# Revit family: 30391 Скамейка для запасных игроков на 5 посадочных мест с навесом «Брейк-5» Хоббика
name_source: partatom
category: Антураж
revit_build: Autodesk Revit 2018 (Build: 20180423_1000(x64)
units: mm (PartAtom-declared; Revit-internal decimal feet)

## family parameters
Всегда вертикально = Да
Источник визуального образа = Геометрия семейства
На основе рабочей плоскости = Нет
Общий = Нет
При загрузке вырезать с полостями = Нет
Точка расчета площади = Нет

## types (1)
- Скамейка для запасных игроков на 5 посадочных мест с навесом «Брейк-5»
    URL = https://hobbyka.ru
    Артикул товара = Арт. 30391
    Высота = 2150 мм
    Группа модели = Мобильные и стационарные трибуны
    Длина = 2840 мм
    Изготовитель = ООО «Хоббика»
    Изображение типоразмера = Скамейка для запасных игроков на 5 посадочных мест с навесом «Брейк-5» Арт 30391.jpg
    Материал изделия = Сталь, поликарбонат, пластик
    Описание = Скамейка для запасных игроков на 5 посадочных мест с навесом «Брейк-5»
    Цвет каркаса = Сталь
    Цвет крыши = Поликарбонат
    Цвет сидений = Красный
    Ширина = 1460 мм

## geometry (parser evidence)
native form markers: Sweep x3
no freeform markers — native parametric forms only
